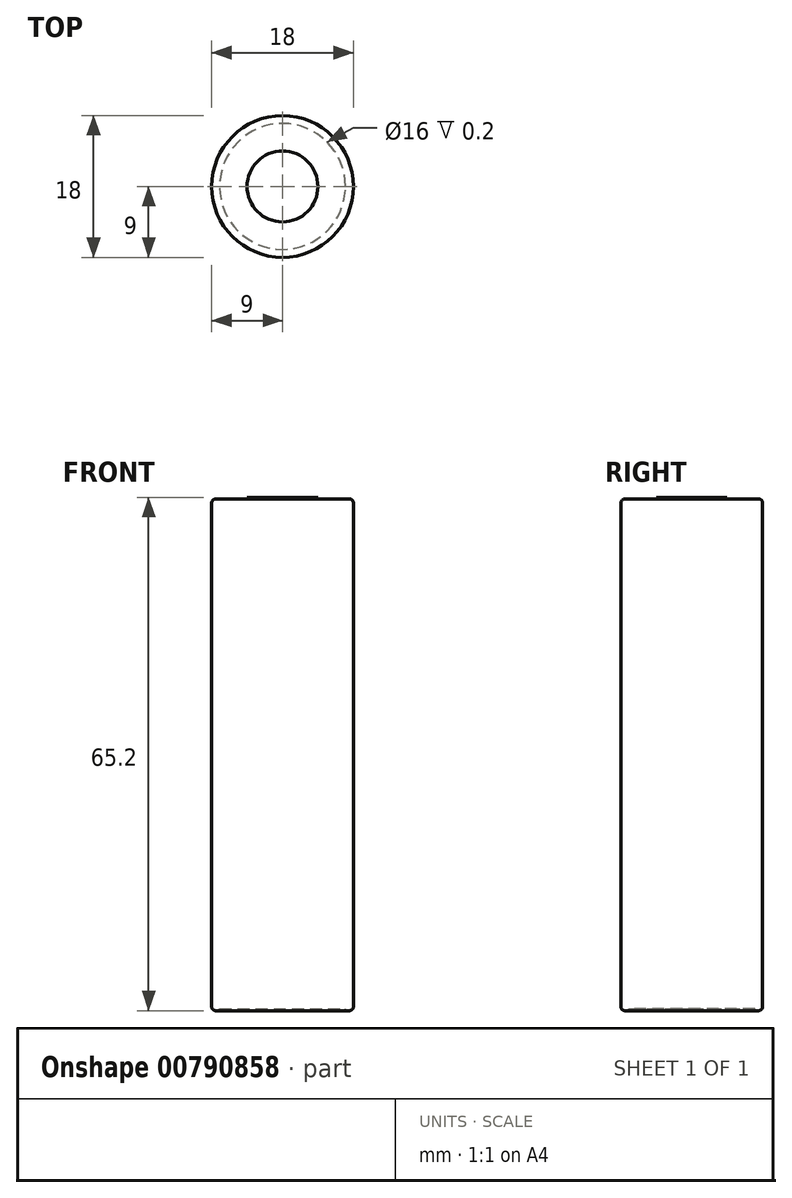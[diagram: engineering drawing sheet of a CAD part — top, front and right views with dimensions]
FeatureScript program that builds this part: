
annotation { "Feature Type Name" : "Feature", "Feature Type Description" : "" }
export const myFeature = defineFeature(function(context is Context, id is Id, definition is map)
    precondition{}
    {
        {
            var Q0;
            Q0=qCreatedBy(makeId("Top.planeOp"),FACE);
            var sketch = newSketch(context, id + "F0", { "sketchPlane" : qUnion([Q0])});
            skCircle(sketch, "E0", {"center": v(0, 0) * mm, "radius": 9 * mm});
            skSolve(sketch);
        }
        {
            var Q0;
            Q0 = qSketchRegion(id + "F0", true);
            extrude(context, id + "F1", {"entities" : qUnion([Q0]), "depth" : 65 * mm, "offsetDistance" : 25 * mm});
        }
        {
            var Q0;
            Q0=makeQuery(id+"F1.opExtrude","CAP_FACE",FACE,{"disambiguationData":[OSD([sQuery(id+"F0.wireOp",EDGE,"E0")])],"isStart":false});
            var sketch = newSketch(context, id + "F2", { "sketchPlane" : qUnion([Q0])});
            skCircle(sketch, "E1", {"center": v(0, 0) * mm, "radius": 4.5 * mm});
            skSolve(sketch);
        }
        {
            var Q0;
            Q0 = qSketchRegion(id + "F2", true);
            extrude(context, id + "F3", {"entities" : qUnion([Q0]), "depth" : 0.2 * mm, "offsetDistance" : 25 * mm});
        }
        {
            var Q0;
            Q0=makeQuery(id+"F1.opExtrude","CAP_FACE",FACE,{"disambiguationData":[OSD([sQuery(id+"F0.wireOp",EDGE,"E0")])],"isStart":true});
            var sketch = newSketch(context, id + "F4", { "sketchPlane" : qUnion([Q0])});
            skCircle(sketch, "E2", {"center": v(0, 0) * mm, "radius": 8 * mm});
            skSolve(sketch);
        }
        {
            var Q0;
            Q0 = qSketchRegion(id + "F4", true);
            extrude(context, id + "F5", {"entities" : qUnion([Q0]), "operationType" : NewBodyOperationType.REMOVE, "oppositeDirection" : true, "depth" : 0.2 * mm, "offsetDistance" : 25 * mm});
        }
        {
            var Q0;
            Q0=makeQuery(id+"F5.boolean.opBoolean","COPY",FACE,{"derivedFrom":makeQuery(id+"F5.opExtrude","CAP_FACE",FACE,{"disambiguationData":[OSD([sQuery(id+"F4.wireOp",EDGE,"E2")])],"isStart":false})});
            var sketch = newSketch(context, id + "F6", { "sketchPlane" : qUnion([Q0])});
            skCircle(sketch, "E3", {"center": v(0, 0) * mm, "radius": 8 * mm});
            skSolve(sketch);
        }
        {
            var Q0;
            Q0 = qSketchRegion(id + "F6", true);
            extrude(context, id + "F7", {"entities" : qUnion([Q0]), "depth" : 0.2 * mm, "offsetDistance" : 25 * mm});
        }
        {
            var Q0;
            Q0=makeQuery(id+"F1.opExtrude","CAP_EDGE",EDGE,{"disambiguationData":[OSD([sQuery(id+"F0.wireOp",EDGE,"E0")])],"isStart":false});
            var Q1;
            Q1=makeQuery(id+"F1.opExtrude","CAP_EDGE",EDGE,{"disambiguationData":[OSD([sQuery(id+"F0.wireOp",EDGE,"E0")])],"isStart":true});
            fillet(context, id + "F8", {"entities" : qUnion([Q0, Q1]), "radius" : 0.5 * mm, "tangentPropagation" : true, "allowEdgeOverflow" : false});
        }
    });
